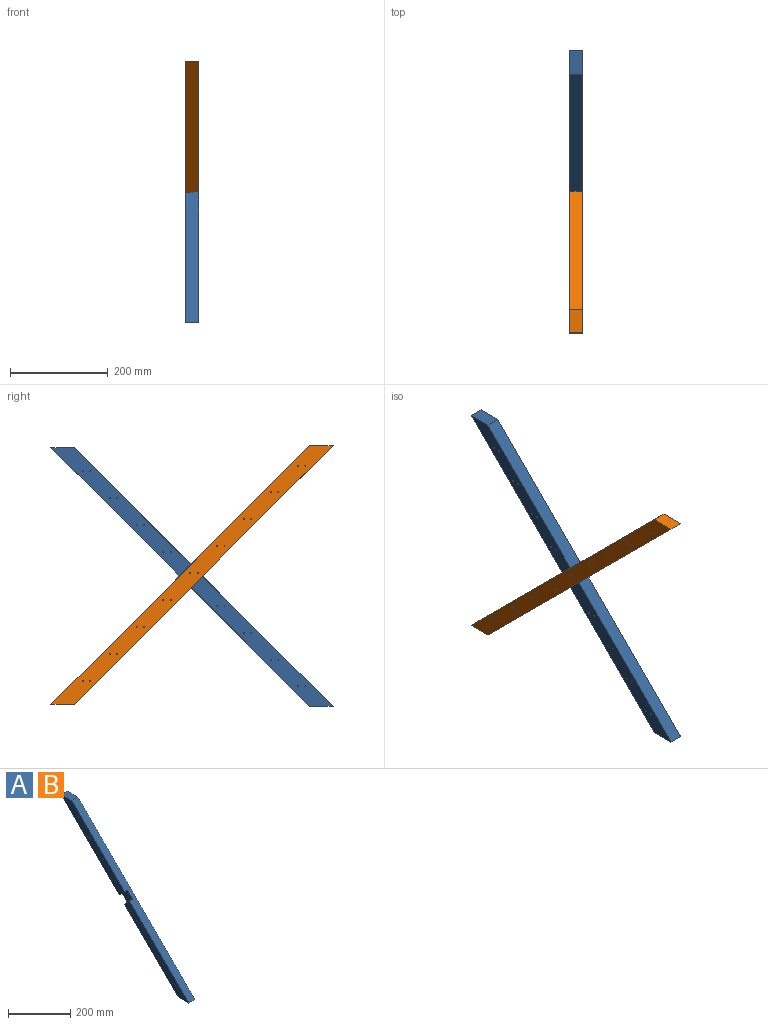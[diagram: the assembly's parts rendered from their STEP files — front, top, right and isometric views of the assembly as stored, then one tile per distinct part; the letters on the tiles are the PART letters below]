
ASSEMBLY  parts=2 mates=1
PART A: 28 faces, bbox 28x578.8x530.7 mm
  f0: plane 287.48x263.43mm, normal (-1,0,0), area 12063.6mm2, adj f1,f3,f4,f8,f20,f21,f22,f23
  f1: plane 530.72x530.72mm, normal (0,-0.71,0.71), area 20539.5mm2, adj f0,f2,f4,f5,f6,f7,f8,f9
  f2: plane 48.08x28mm, normal (0,0,-1), area 1346.3mm2, adj f1,f3,f5,f6
  f3: plane 530.72x530.72mm, normal (0,0.71,-0.71), area 20539.5mm2, adj f0,f2,f4,f5,f6,f7,f8,f9
  f4: plane 48.08x28mm, normal (0,0,1), area 1346.3mm2, adj f0,f1,f3,f5
  f5: plane 578.8x530.72mm, normal (1,0,0), area 25462.2mm2, adj f1,f2,f3,f4,f10,f11,f12,f13
  f6: plane 291.33x267.29mm, normal (-1,0,0), area 12248.9mm2, adj f1,f2,f3,f7,f12,f13,f14,f15
  f7: plane 24.04x24.04mm, normal (0,0.71,0.71), area 476mm2, adj f1,f3,f6,f9
  f8: plane 24.04x24.04mm, normal (0,-0.71,-0.71), area 476mm2, adj f0,f1,f3,f9
  f9: plane 48.08x48.08mm, normal (-1,0,0), area 1149.7mm2, adj f1,f3,f7,f8,f10,f11
  f10: cylinder r=1mm len=14mm, axis (1,0,0), area 88mm2, adj f5,f9
  f11: cylinder r=1mm len=14mm, axis (1,0,0), area 88mm2, adj f5,f9
  f12: cylinder r=1mm len=28mm, axis (1,0,0), area 175.9mm2, adj f5,f6
  f13: cylinder r=1mm len=28mm, axis (1,0,0), area 175.9mm2, adj f5,f6
  f14: cylinder r=1mm len=28mm, axis (1,0,0), area 175.9mm2, adj f5,f6
  f15: cylinder r=1mm len=28mm, axis (1,0,0), area 175.9mm2, adj f5,f6
  f16: cylinder r=1mm len=28mm, axis (1,0,0), area 175.9mm2, adj f5,f6
  f17: cylinder r=1mm len=28mm, axis (1,0,0), area 175.9mm2, adj f5,f6
  f18: cylinder r=1mm len=28mm, axis (1,0,0), area 175.9mm2, adj f5,f6
  f19: cylinder r=1mm len=28mm, axis (1,0,0), area 175.9mm2, adj f5,f6
  f20: cylinder r=1mm len=28mm, axis (1,0,0), area 175.9mm2, adj f0,f5
  f21: cylinder r=1mm len=28mm, axis (1,0,0), area 175.9mm2, adj f0,f5
  f22: cylinder r=1mm len=28mm, axis (1,0,0), area 175.9mm2, adj f0,f5
  f23: cylinder r=1mm len=28mm, axis (1,0,0), area 175.9mm2, adj f0,f5
  f24: cylinder r=1mm len=28mm, axis (1,0,0), area 175.9mm2, adj f0,f5
  f25: cylinder r=1mm len=28mm, axis (1,0,0), area 175.9mm2, adj f0,f5
  f26: cylinder r=1mm len=28mm, axis (1,0,0), area 175.9mm2, adj f0,f5
  f27: cylinder r=1mm len=28mm, axis (1,0,0), area 175.9mm2, adj f0,f5
PART B: same geometry as A
PLACE A t=(-182.05,-11.63,-39.9)mm
PLACE B rot(axis=(0,1,0),180deg) t=(-154.05,-11.63,494.73)mm
MATE fastened B.f9 <-> A.f9  axis (1,0,0) through (-168.05,54.73,227.41)mm
